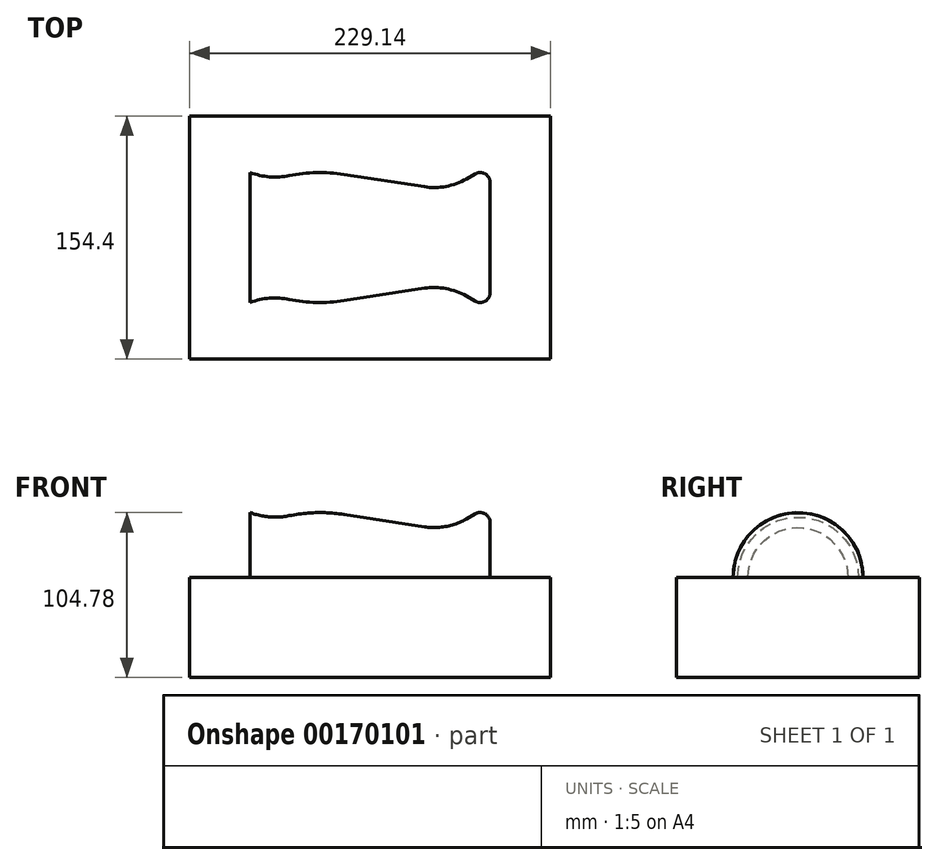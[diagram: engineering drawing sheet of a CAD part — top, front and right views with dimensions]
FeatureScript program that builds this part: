
annotation { "Feature Type Name" : "Feature", "Feature Type Description" : "" }
export const myFeature = defineFeature(function(context is Context, id is Id, definition is map)
    precondition{}
    {
        {
            var Q0;
            Q0=qCreatedBy(makeId("Top.planeOp"),FACE);
            var sketch = newSketch(context, id + "F0", { "sketchPlane" : qUnion([Q0])});
            skLineSegment(sketch, "E0", {"start": v(-76.2, 0) * mm, "end": v(76.2, 0) * mm});
            skLineSegment(sketch, "E1", {"start": v(-76.2, 0) * mm, "end": v(-76.2, 19.05) * mm, "construction": true});
            skLineSegment(sketch, "E2", {"start": v(-76.2, 19.05) * mm, "end": v(76.2, 19.05) * mm, "construction": true});
            skLineSegment(sketch, "E3", {"start": v(-76.2, 19.05) * mm, "end": v(-76.2, 41.28) * mm, "construction": true});
            skLineSegment(sketch, "E4", {"start": v(-76.2, 41.28) * mm, "end": v(76.2, 41.27) * mm, "construction": true});
            skPoint(sketch, "E5", {"position": v(-31.75, 41.28) * mm});
            skLineSegment(sketch, "E6", {"start": v(76.2, 0) * mm, "end": v(76.2, 19.05) * mm, "construction": true});
            skLineSegment(sketch, "E7", {"start": v(-76.2, 31.75) * mm, "end": v(76.2, 31.75) * mm, "construction": true});
            skLineSegment(sketch, "E8", {"start": v(76.2, 19.05) * mm, "end": v(76.2, 41.28) * mm, "construction": true});
            skPoint(sketch, "E9", {"position": v(40.64, 31.75) * mm});
            skLineSegment(sketch, "E10", {"start": v(76.2, 0) * mm, "end": v(76.2, 34.92) * mm});
            skArc(sketch, "E11", {"start": v(76.2, 34.92) * mm, "mid": v(73.03, 40.42) * mm, "end": v(66.69, 40.43) * mm});
            skLineSegment(sketch, "E12", {"start": v(61.04, 37.2) * mm, "end": v(66.69, 40.43) * mm});
            skLineSegment(sketch, "E13", {"start": v(-16.73, 40.12) * mm, "end": v(34.39, 32.23) * mm});
            skArc(sketch, "E14", {"start": v(34.39, 32.23) * mm, "mid": v(48.14, 32.44) * mm, "end": v(61.04, 37.2) * mm});
            skArc(sketch, "E15", {"start": v(-16.73, 40.12) * mm, "mid": v(-34.1, 41.25) * mm, "end": v(-51.4, 39.3) * mm});
            skArc(sketch, "E16", {"start": v(-76.2, 41.28) * mm, "mid": v(-63.94, 38.53) * mm, "end": v(-51.4, 39.3) * mm});
            skLineSegment(sketch, "E17", {"start": v(-76.2, 41.28) * mm, "end": v(-76.2, 0) * mm});
            skSolve(sketch);
        }
        {
            var Q0;
            Q0=makeQuery(id+"F0.imprint","IMPRINT",FACE,{"disambiguationData":[TD([[makeQuery(id+"F0.imprint","IMPRINT",EDGE,{"derivedFrom":sQuery(id+"F0.wireOp",EDGE,"E0")}),1.0]])]});
            var Q1;
            Q1=sQuery(id+"F0.wireOp",EDGE,"E0");
            revolve(context, id + "F1", {"entities" : qUnion([Q0]), "axis" : qUnion([Q1]), "revolveType" : RevolveType.FULL});
        }
        {
            var Q0;
            Q0=qCreatedBy(makeId("Top.planeOp"),FACE);
            var sketch = newSketch(context, id + "F2", { "sketchPlane" : qUnion([Q0])});
            skLineSegment(sketch, "E18.bottom", {"start": v(114.57, 77.2) * mm, "end": v(-114.57, 77.2) * mm});
            skLineSegment(sketch, "E18.top", {"start": v(114.57, -77.2) * mm, "end": v(-114.57, -77.2) * mm});
            skLineSegment(sketch, "E18.left", {"start": v(114.57, 77.2) * mm, "end": v(114.57, -77.2) * mm});
            skLineSegment(sketch, "E18.right", {"start": v(-114.57, 77.2) * mm, "end": v(-114.57, -77.2) * mm});
            skPoint(sketch, "E18.middle", {"position": v(0, 0) * mm});
            skSolve(sketch);
        }
        {
            var Q0;
            Q0 = qSketchRegion(id + "F2", true);
            extrude(context, id + "F3", {"entities" : qUnion([Q0]), "operationType" : NewBodyOperationType.ADD, "oppositeDirection" : true, "depth" : 63.5 * mm});
        }
    });
